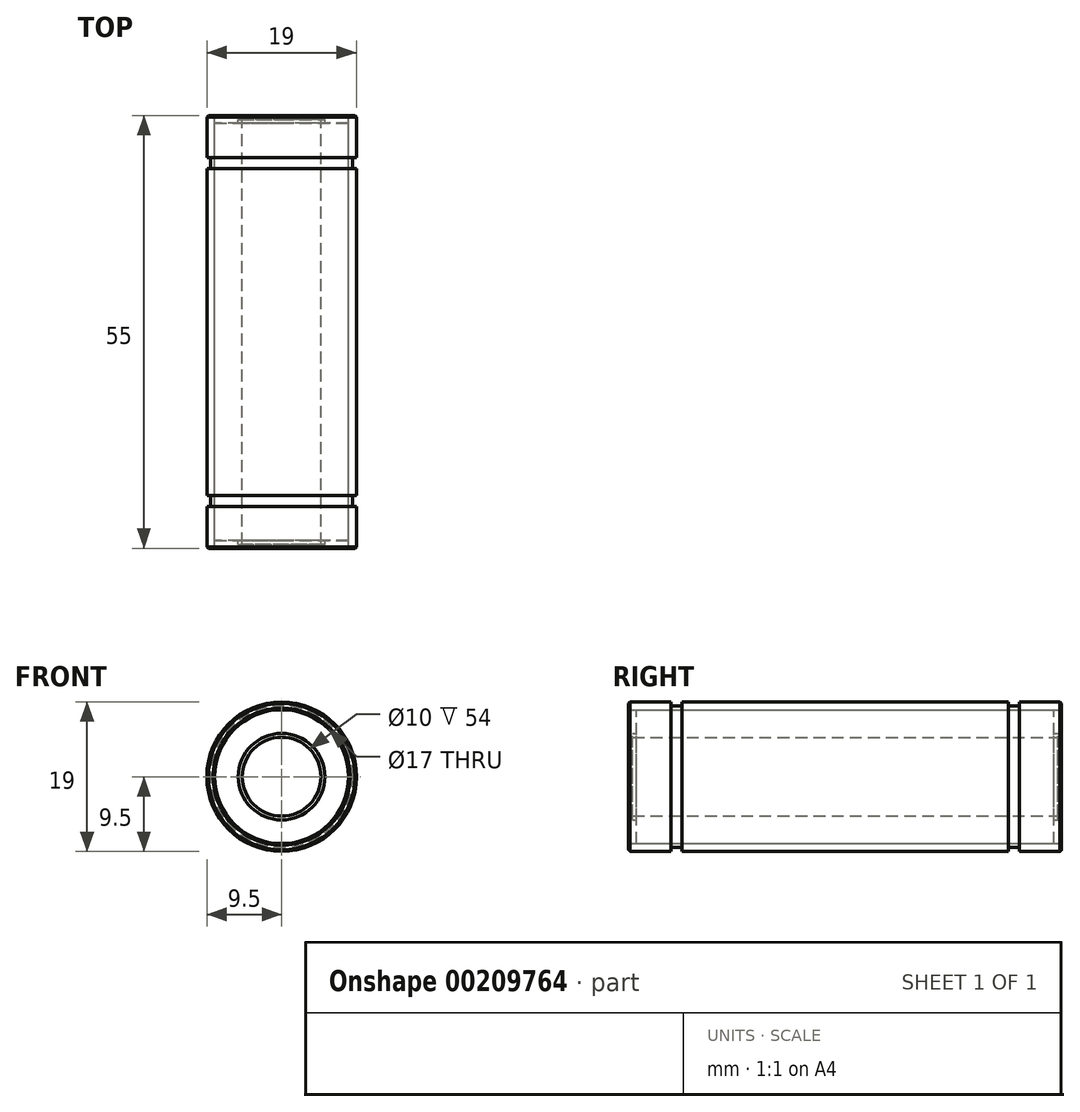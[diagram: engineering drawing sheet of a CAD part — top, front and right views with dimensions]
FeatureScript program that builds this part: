
annotation { "Feature Type Name" : "Feature", "Feature Type Description" : "" }
export const myFeature = defineFeature(function(context is Context, id is Id, definition is map)
    precondition{}
    {
        {
            var Q0;
            Q0=qCreatedBy(makeId("Front.planeOp"),FACE);
            var sketch = newSketch(context, id + "F0", { "sketchPlane" : qUnion([Q0])});
            skCircle(sketch, "E0", {"center": v(0, 0) * mm, "radius": 9.5 * mm});
            skCircle(sketch, "E1", {"center": v(0, 0) * mm, "radius": 8.5 * mm});
            skCircle(sketch, "E2", {"center": v(0, 0) * mm, "radius": 5 * mm});
            skCircle(sketch, "E3", {"center": v(0, 0) * mm, "radius": 5.5 * mm});
            skSolve(sketch);
        }
        {
            var Q0;
            Q0=makeQuery(id+"F0.imprint","IMPRINT",FACE,{"disambiguationData":[TD([[makeQuery(id+"F0.imprint","IMPRINT",EDGE,{"derivedFrom":sQuery(id+"F0.wireOp",EDGE,"E0")}),1.0]])]});
            extrude(context, id + "F1", {"entities" : qUnion([Q0]), "endBound" : BoundingType.SYMMETRIC, "depth" : 55 * mm});
        }
        {
            var Q0;
            Q0=makeQuery(id+"F0.imprint","IMPRINT",FACE,{"disambiguationData":[TD([[makeQuery(id+"F0.imprint","IMPRINT",EDGE,{"derivedFrom":sQuery(id+"F0.wireOp",EDGE,"E1")}),1.0]])]});
            extrude(context, id + "F2", {"entities" : qUnion([Q0]), "endBound" : BoundingType.SYMMETRIC, "depth" : 53 * mm});
        }
        {
            var Q0;
            Q0=makeQuery(id+"F0.imprint","IMPRINT",FACE,{"disambiguationData":[TD([[makeQuery(id+"F0.imprint","IMPRINT",EDGE,{"derivedFrom":sQuery(id+"F0.wireOp",EDGE,"E2")}),-1.0]])]});
            extrude(context, id + "F3", {"entities" : qUnion([Q0]), "operationType" : NewBodyOperationType.ADD, "endBound" : BoundingType.SYMMETRIC, "depth" : 54 * mm});
        }
        {
            var Q0;
            Q0=makeQuery(id+"F1.opExtrude","CAP_FACE",FACE,{"disambiguationData":[OSD([sQuery(id+"F0.wireOp",EDGE,"E0"),sQuery(id+"F0.wireOp",EDGE,"E1")])],"isStart":false});
            var Q1;
            Q1=makeQuery(id+"F1.opExtrude","CAP_FACE",FACE,{"disambiguationData":[OSD([sQuery(id+"F0.wireOp",EDGE,"E0"),sQuery(id+"F0.wireOp",EDGE,"E1")])],"isStart":true});
            chamfer(context, id + "F4", {"entities" : qUnion([Q0, Q1]), "width" : .2 * mm, "tangentPropagation" : true});
        }
        {
            var Q0;
            Q0=qCreatedBy(makeId("Right.planeOp"),FACE);
            var sketch = newSketch(context, id + "F5", { "sketchPlane" : qUnion([Q0])});
            skLineSegment(sketch, "E4", {"start": v(-27.5, 0) * mm, "end": v(27.5, 0) * mm, "construction": true});
            skLineSegment(sketch, "E5", {"start": v(0, 0) * mm, "end": v(0, 7.48) * mm, "construction": true});
            skLineSegment(sketch, "E6.bottom", {"start": v(-22.15, 10) * mm, "end": v(-20.75, 10) * mm});
            skLineSegment(sketch, "E6.top", {"start": v(-22.15, 9) * mm, "end": v(-20.75, 9) * mm});
            skLineSegment(sketch, "E6.left", {"start": v(-22.15, 10) * mm, "end": v(-22.15, 9) * mm});
            skLineSegment(sketch, "E6.right", {"start": v(-20.75, 10) * mm, "end": v(-20.75, 9) * mm});
            skLineSegment(sketch, "E7.MirrorCS", {"start": v(20.75, 10) * mm, "end": v(20.75, 9) * mm});
            skLineSegment(sketch, "E8.MirrorCS", {"start": v(22.15, 10) * mm, "end": v(22.15, 9) * mm});
            skLineSegment(sketch, "E9.MirrorCS", {"start": v(22.15, 9) * mm, "end": v(20.75, 9) * mm});
            skLineSegment(sketch, "E10.MirrorCS", {"start": v(22.15, 10) * mm, "end": v(20.75, 10) * mm});
            skSolve(sketch);
        }
        {
            var Q0;
            Q0=makeQuery(id+"F5.imprint","IMPRINT",FACE,{"disambiguationData":[TD([[makeQuery(id+"F5.imprint","IMPRINT",EDGE,{"derivedFrom":sQuery(id+"F5.wireOp",EDGE,"E6.bottom")}),-1.0]])]});
            var Q1;
            Q1=makeQuery(id+"F5.imprint","IMPRINT",FACE,{"disambiguationData":[TD([[makeQuery(id+"F5.imprint","IMPRINT",EDGE,{"derivedFrom":sQuery(id+"F5.wireOp",EDGE,"E7.MirrorCS")}),1.0]])]});
            var Q2;
            Q2=sQuery(id+"F5.wireOp",EDGE,"E4");
            revolve(context, id + "F6", {"operationType" : NewBodyOperationType.REMOVE, "entities" : qUnion([Q0, Q1]), "axis" : qUnion([Q2]), "revolveType" : RevolveType.FULL, "oppositeDirection" : true});
        }
    });
